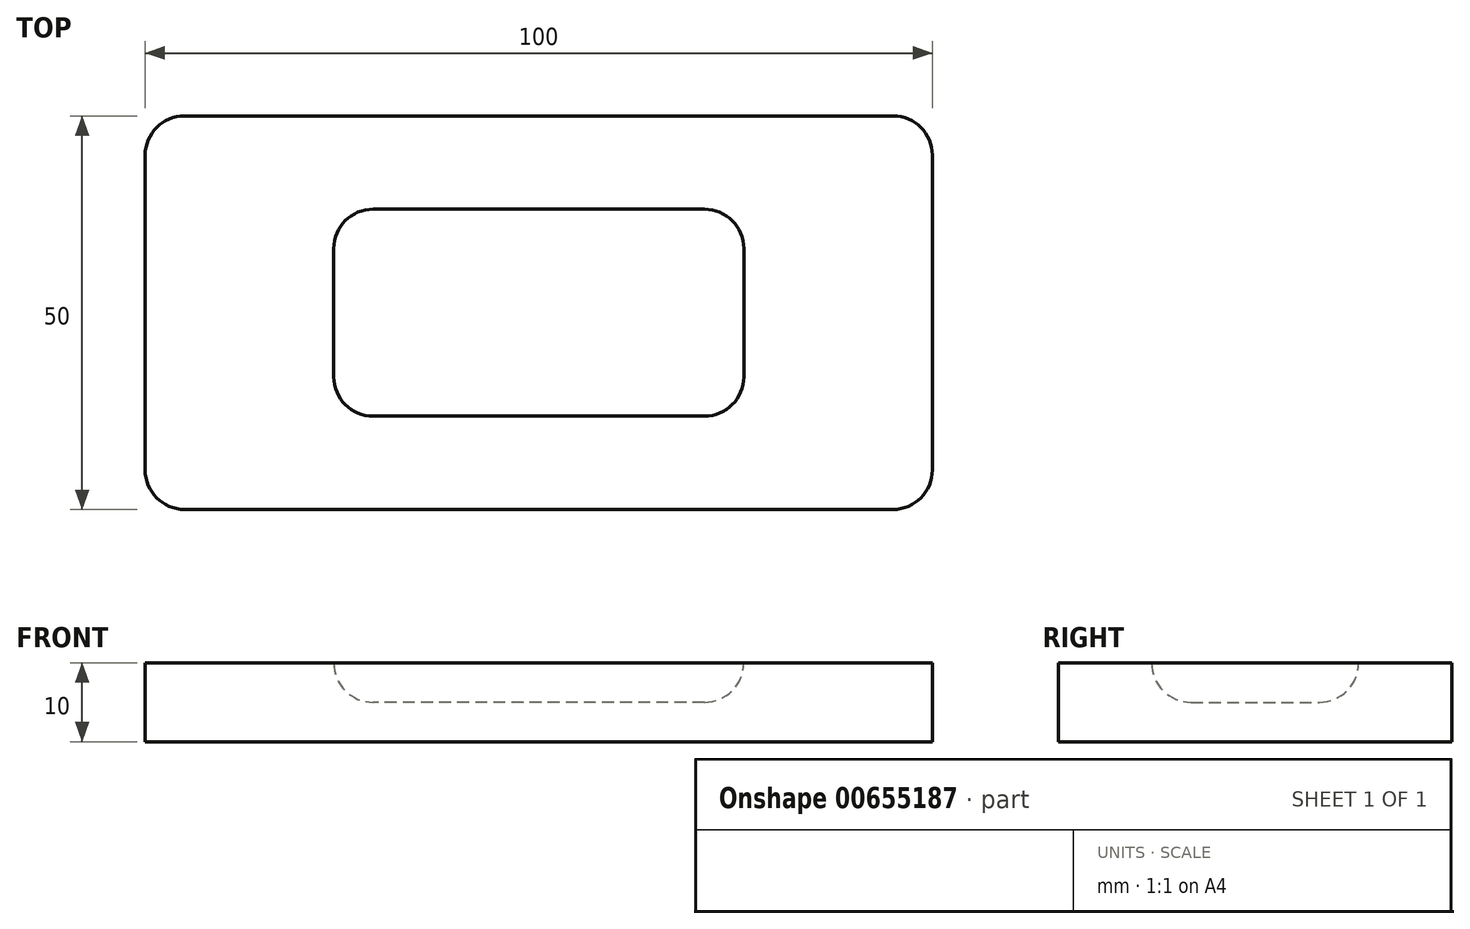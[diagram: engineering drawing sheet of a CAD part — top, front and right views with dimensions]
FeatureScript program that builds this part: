
annotation { "Feature Type Name" : "Feature", "Feature Type Description" : "" }
export const myFeature = defineFeature(function(context is Context, id is Id, definition is map)
    precondition{}
    {
        {
            var Q0;
            Q0=qCreatedBy(makeId("Top.planeOp"),FACE);
            var sketch = newSketch(context, id + "F0", { "sketchPlane" : qUnion([Q0])});
            skLineSegment(sketch, "E0.bottom", {"start": v(50, -25) * mm, "end": v(-50, -25) * mm});
            skLineSegment(sketch, "E0.top", {"start": v(50, 25) * mm, "end": v(-50, 25) * mm});
            skLineSegment(sketch, "E0.left", {"start": v(50, -25) * mm, "end": v(50, 25) * mm});
            skLineSegment(sketch, "E0.right", {"start": v(-50, -25) * mm, "end": v(-50, 25) * mm});
            skPoint(sketch, "E0.middle", {"position": v(0, 0) * mm});
            skSolve(sketch);
        }
        {
            var Q0;
            Q0=makeQuery(id+"F0.imprint","IMPRINT",FACE,{"disambiguationData":[TD([[makeQuery(id+"F0.imprint","IMPRINT",EDGE,{"derivedFrom":sQuery(id+"F0.wireOp",EDGE,"E0.bottom")}),-1.0]])]});
            extrude(context, id + "F1", {"entities" : qUnion([Q0]), "depth" : 10 * mm, "offsetDistance" : 25 * mm});
        }
        {
            var Q0;
            Q0=makeQuery(id+"F1.opExtrude","SWEPT_EDGE",EDGE,{"disambiguationData":[OSD([sQuery(id+"F0.wireOp",EDGE,"E0.bottom"),sQuery(id+"F0.wireOp",EDGE,"E0.right")])]});
            var Q1;
            Q1=makeQuery(id+"F1.opExtrude","SWEPT_EDGE",EDGE,{"disambiguationData":[OSD([sQuery(id+"F0.wireOp",EDGE,"E0.top"),sQuery(id+"F0.wireOp",EDGE,"E0.right")])]});
            var Q2;
            Q2=makeQuery(id+"F1.opExtrude","SWEPT_EDGE",EDGE,{"disambiguationData":[OSD([sQuery(id+"F0.wireOp",EDGE,"E0.bottom"),sQuery(id+"F0.wireOp",EDGE,"E0.left")])]});
            var Q3;
            Q3=makeQuery(id+"F1.opExtrude","SWEPT_EDGE",EDGE,{"disambiguationData":[OSD([sQuery(id+"F0.wireOp",EDGE,"E0.top"),sQuery(id+"F0.wireOp",EDGE,"E0.left")])]});
            fillet(context, id + "F2", {"entities" : qUnion([Q0, Q1, Q2, Q3]), "radius" : 5 * mm, "tangentPropagation" : true, "allowEdgeOverflow" : false});
        }
        {
            var Q0;
            Q0=makeQuery(id+"F1.opExtrude","CAP_FACE",FACE,{"disambiguationData":[OSD([sQuery(id+"F0.wireOp",EDGE,"E0.bottom"),sQuery(id+"F0.wireOp",EDGE,"E0.top"),sQuery(id+"F0.wireOp",EDGE,"E0.left"),sQuery(id+"F0.wireOp",EDGE,"E0.right")])],"isStart":false});
            var sketch = newSketch(context, id + "F3", { "sketchPlane" : qUnion([Q0])});
            skLineSegment(sketch, "E1.bottom", {"start": v(26.04, -13.15) * mm, "end": v(-26.04, -13.15) * mm});
            skLineSegment(sketch, "E1.top", {"start": v(26.04, 13.15) * mm, "end": v(-26.04, 13.15) * mm});
            skLineSegment(sketch, "E1.left", {"start": v(26.04, -13.15) * mm, "end": v(26.04, 13.15) * mm});
            skLineSegment(sketch, "E1.right", {"start": v(-26.04, -13.15) * mm, "end": v(-26.04, 13.15) * mm});
            skPoint(sketch, "E1.middle", {"position": v(0, 0) * mm});
            skSolve(sketch);
        }
        {
            var Q0;
            Q0=makeQuery(id+"F3.imprint","IMPRINT",FACE,{"disambiguationData":[TD([[makeQuery(id+"F3.imprint","IMPRINT",EDGE,{"derivedFrom":sQuery(id+"F3.wireOp",EDGE,"E1.bottom")}),-1.0]])]});
            extrude(context, id + "F4", {"entities" : qUnion([Q0]), "operationType" : NewBodyOperationType.REMOVE, "oppositeDirection" : true, "depth" : 5 * mm, "offsetDistance" : 25 * mm});
        }
        {
            var Q0;
            Q0=makeQuery(id+"F4.boolean.opBoolean","COPY",EDGE,{"derivedFrom":makeQuery(id+"F4.opExtrude","SWEPT_EDGE",EDGE,{"disambiguationData":[OSD([sQuery(id+"F3.wireOp",EDGE,"E1.top"),sQuery(id+"F3.wireOp",EDGE,"E1.right")])]})});
            var Q1;
            Q1=makeQuery(id+"F4.boolean.opBoolean","COPY",EDGE,{"derivedFrom":makeQuery(id+"F4.opExtrude","SWEPT_EDGE",EDGE,{"disambiguationData":[OSD([sQuery(id+"F3.wireOp",EDGE,"E1.top"),sQuery(id+"F3.wireOp",EDGE,"E1.left")])]})});
            var Q2;
            Q2=makeQuery(id+"F4.boolean.opBoolean","COPY",EDGE,{"derivedFrom":makeQuery(id+"F4.opExtrude","SWEPT_EDGE",EDGE,{"disambiguationData":[OSD([sQuery(id+"F3.wireOp",EDGE,"E1.bottom"),sQuery(id+"F3.wireOp",EDGE,"E1.left")])]})});
            var Q3;
            Q3=makeQuery(id+"F4.boolean.opBoolean","COPY",EDGE,{"derivedFrom":makeQuery(id+"F4.opExtrude","SWEPT_EDGE",EDGE,{"disambiguationData":[OSD([sQuery(id+"F3.wireOp",EDGE,"E1.bottom"),sQuery(id+"F3.wireOp",EDGE,"E1.right")])]})});
            fillet(context, id + "F5", {"entities" : qUnion([Q0, Q1, Q2, Q3]), "radius" : 5 * mm, "tangentPropagation" : true, "allowEdgeOverflow" : false});
        }
        {
            var Q0;
            Q0=makeQuery(id+"F4.boolean.opBoolean","COPY",FACE,{"derivedFrom":makeQuery(id+"F4.opExtrude","CAP_FACE",FACE,{"disambiguationData":[OSD([sQuery(id+"F3.wireOp",EDGE,"E1.bottom"),sQuery(id+"F3.wireOp",EDGE,"E1.top"),sQuery(id+"F3.wireOp",EDGE,"E1.left"),sQuery(id+"F3.wireOp",EDGE,"E1.right")])],"isStart":false})});
            fillet(context, id + "F6", {"entities" : qUnion([Q0]), "radius" : 5 * mm, "tangentPropagation" : true, "allowEdgeOverflow" : false});
        }
    });
